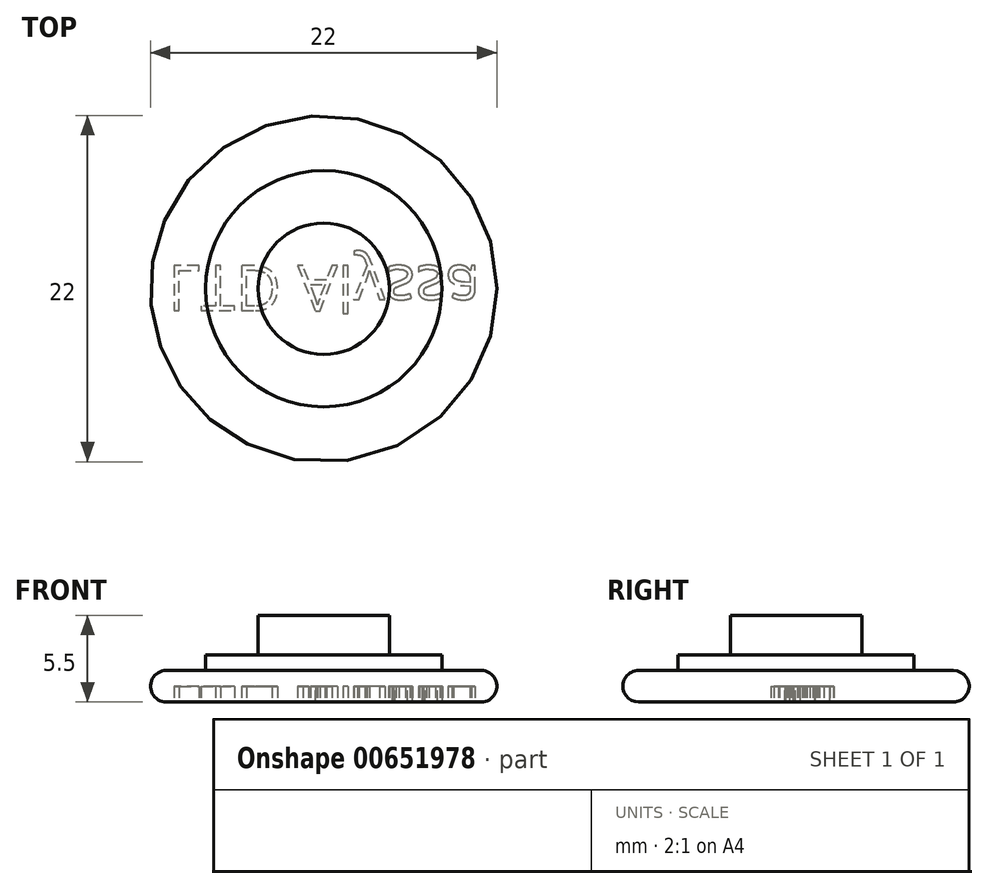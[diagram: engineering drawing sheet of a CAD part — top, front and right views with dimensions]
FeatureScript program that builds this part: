
annotation { "Feature Type Name" : "Feature", "Feature Type Description" : "" }
export const myFeature = defineFeature(function(context is Context, id is Id, definition is map)
    precondition{}
    {
        {
            var Q0;
            Q0=qCreatedBy(makeId("Top.planeOp"),FACE);
            var sketch = newSketch(context, id + "F0", { "sketchPlane" : qUnion([Q0])});
            skCircle(sketch, "E0", {"center": v(0, 0) * mm, "radius": 11 * mm});
            skCircle(sketch, "E1", {"center": v(0, 0) * mm, "radius": 7.5 * mm});
            skCircle(sketch, "E2", {"center": v(0, 0) * mm, "radius": 4.17 * mm});
            skSolve(sketch);
        }
        {
            var Q0;
            Q0=makeQuery(id+"F0.imprint","IMPRINT",FACE,{"disambiguationData":[TD([[makeQuery(id+"F0.imprint","IMPRINT",EDGE,{"derivedFrom":sQuery(id+"F0.wireOp",EDGE,"E0")}),1.0]])]});
            extrude(context, id + "F1", {"entities" : qUnion([Q0]), "depth" : 2 * mm, "offsetDistance" : 25 * mm});
        }
        {
            var Q0;
            Q0=makeQuery(id+"F0.imprint","IMPRINT",FACE,{"disambiguationData":[TD([[makeQuery(id+"F0.imprint","IMPRINT",EDGE,{"derivedFrom":sQuery(id+"F0.wireOp",EDGE,"E1")}),1.0]])]});
            extrude(context, id + "F2", {"entities" : qUnion([Q0]), "operationType" : NewBodyOperationType.ADD, "depth" : 3 * mm, "offsetDistance" : 25 * mm});
        }
        {
            var Q0;
            Q0=makeQuery(id+"F0.imprint","IMPRINT",FACE,{"disambiguationData":[TD([[makeQuery(id+"F0.imprint","IMPRINT",EDGE,{"derivedFrom":sQuery(id+"F0.wireOp",EDGE,"E2")}),1.0]])]});
            extrude(context, id + "F3", {"entities" : qUnion([Q0]), "operationType" : NewBodyOperationType.ADD, "depth" : 5.5 * mm, "offsetDistance" : 25 * mm});
        }
        {
            var Q0;
            Q0=makeQuery(id+"F1.opExtrude","CAP_EDGE",EDGE,{"disambiguationData":[OSD([sQuery(id+"F0.wireOp",EDGE,"E0")])],"isStart":false});
            var Q1;
            Q1=makeQuery(id+"F1.opExtrude","CAP_EDGE",EDGE,{"disambiguationData":[OSD([sQuery(id+"F0.wireOp",EDGE,"E0")])],"isStart":true});
            fillet(context, id + "F4", {"entities" : qUnion([Q0, Q1]), "radius" : 1 * mm, "tangentPropagation" : true, "allowEdgeOverflow" : false});
        }
        {
            var Q0;
            {var subQ0=sQuery(id+"F0.wireOp",EDGE,"E2");var subQ1=sQuery(id+"F0.wireOp",EDGE,"E1");Q0=makeQuery(id+"F3.boolean.opBoolean","MERGE",FACE,{"derivedFrom":[makeQuery(id+"F2.boolean.opBoolean","MERGE",FACE,{"derivedFrom":[makeQuery(id+"F1.opExtrude","CAP_FACE",FACE,{"disambiguationData":[OSD([sQuery(id+"F0.wireOp",EDGE,"E0"),subQ1])],"isStart":true}),makeQuery(id+"F2.opExtrude","CAP_FACE",FACE,{"disambiguationData":[OSD([subQ1,subQ0])],"isStart":true})]}),makeQuery(id+"F3.opExtrude","CAP_FACE",FACE,{"disambiguationData":[OSD([subQ0])],"isStart":true})]});}
            var sketch = newSketch(context, id + "F5", { "sketchPlane" : qUnion([Q0])});
            skText(sketch, "E3", { "text": "LTD Alyssa", "fontName": "OpenSans-Regular.ttf"});
            const initialGuessF5  = {"E3": [-0.0099, -0.00146, 1, 0, 0.00288]};
            skSetInitialGuess(sketch, initialGuessF5);
            skSolve(sketch);
        }
        {
            var Q0;
            Q0 = qSketchRegion(id + "F5", true);
            extrude(context, id + "F6", {"entities" : qUnion([Q0]), "operationType" : NewBodyOperationType.REMOVE, "oppositeDirection" : true, "depth" : 1 * mm, "offsetDistance" : 25 * mm});
        }
    });
